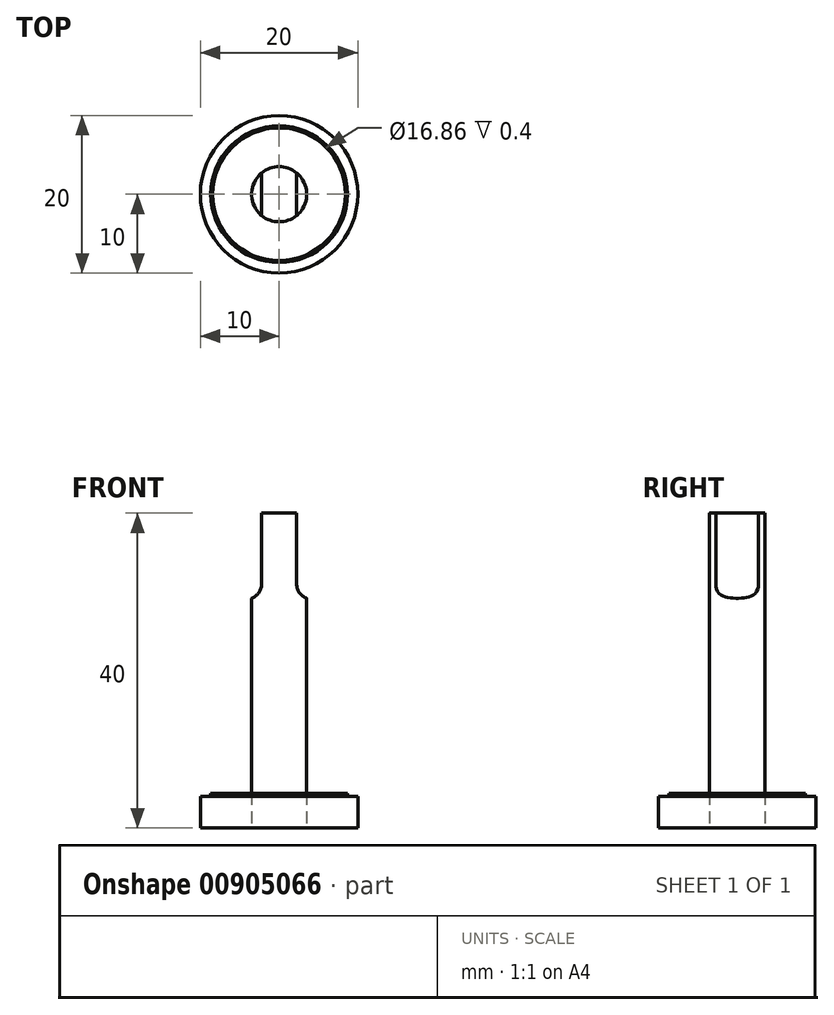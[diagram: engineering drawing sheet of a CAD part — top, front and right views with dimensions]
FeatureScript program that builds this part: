
annotation { "Feature Type Name" : "Feature", "Feature Type Description" : "" }
export const myFeature = defineFeature(function(context is Context, id is Id, definition is map)
    precondition{}
    {
        {
            var Q0;
            Q0=qCreatedBy(makeId("Top.planeOp"),FACE);
            var sketch = newSketch(context, id + "F0", { "sketchPlane" : qUnion([Q0])});
            skCircle(sketch, "E0", {"center": v(0, 0) * mm, "radius": 10 * mm});
            skCircle(sketch, "E1", {"center": v(0, 0) * mm, "radius": 3.5 * mm});
            skSolve(sketch);
        }
        {
            var Q0;
            Q0=makeQuery(id+"F0.imprint","IMPRINT",FACE,{"disambiguationData":[TD([[makeQuery(id+"F0.imprint","IMPRINT",EDGE,{"derivedFrom":sQuery(id+"F0.wireOp",EDGE,"E0")}),1.0]])]});
            var Q1;
            Q1=makeQuery(id+"F0.imprint","IMPRINT",FACE,{"disambiguationData":[TD([[makeQuery(id+"F0.imprint","IMPRINT",EDGE,{"derivedFrom":sQuery(id+"F0.wireOp",EDGE,"E1")}),-1.0]])]});
            var Q2;
            Q2=makeQuery(id+"F0.imprint","IMPRINT",FACE,{"disambiguationData":[TD([[makeQuery(id+"F0.imprint","IMPRINT",EDGE,{"derivedFrom":sQuery(id+"F0.wireOp",EDGE,"UNOtp6jB-zNbs-lB1D-Yq4t-WwCaiyIfWIL7")}),1.0]])]});
            var Q3;
            Q3=makeQuery(id+"F0.imprint","IMPRINT",FACE,{"disambiguationData":[TD([[makeQuery(id+"F0.imprint","IMPRINT",EDGE,{"derivedFrom":sQuery(id+"F0.wireOp",EDGE,"E1")}),1.0]])]});
            extrude(context, id + "F1", {"entities" : qUnion([Q0, Q1, Q2, Q3]), "depth" : 4 * mm, "offsetDistance" : 25 * mm});
        }
        {
            var Q0;
            Q0=makeQuery(id+"F0.imprint","IMPRINT",FACE,{"disambiguationData":[TD([[makeQuery(id+"F0.imprint","IMPRINT",EDGE,{"derivedFrom":sQuery(id+"F0.wireOp",EDGE,"E1")}),1.0]])]});
            extrude(context, id + "F2", {"entities" : qUnion([Q0]), "depth" : 40 * mm, "offsetDistance" : 25 * mm});
        }
        {
            var Q0;
            Q0=makeQuery(id+"F1.opExtrude","CAP_FACE",FACE,{"disambiguationData":[OSD([sQuery(id+"F0.wireOp",EDGE,"E0")])],"isStart":false});
            var sketch = newSketch(context, id + "F3", { "sketchPlane" : qUnion([Q0])});
            skCircle(sketch, "E2", {"center": v(0, 0) * mm, "radius": 8.68 * mm});
            skCircle(sketch, "E3", {"center": v(0, 0) * mm, "radius": 8.43 * mm});
            skSolve(sketch);
        }
        {
            var Q0;
            Q0=makeQuery(id+"F0.imprint","IMPRINT",FACE,{"disambiguationData":[TD([[makeQuery(id+"F0.imprint","IMPRINT",EDGE,{"derivedFrom":sQuery(id+"F0.wireOp",EDGE,"UNOtp6jB-zNbs-lB1D-Yq4t-WwCaiyIfWIL7")}),1.0]])]});
            var Q1;
            Q1 = qSketchRegion(id + "F3", true);
            extrude(context, id + "F4", {"entities" : qUnion([Q0, Q1]), "depth" : .4 * mm, "offsetDistance" : 25 * mm});
        }
        {
            var Q0;
            Q0=qCreatedBy(makeId("Front.planeOp"),FACE);
            var sketch = newSketch(context, id + "F5", { "sketchPlane" : qUnion([Q0])});
            skLineSegment(sketch, "E4.bottom", {"start": v(2.21, 41.1) * mm, "end": v(6.16, 41.1) * mm});
            skLineSegment(sketch, "E4.top", {"start": v(2.21, 31.03) * mm, "end": v(6.16, 31.03) * mm});
            skLineSegment(sketch, "E4.left", {"start": v(2.21, 41.1) * mm, "end": v(2.21, 31.03) * mm});
            skLineSegment(sketch, "E4.right", {"start": v(6.16, 41.1) * mm, "end": v(6.16, 31.03) * mm});
            skArc(sketch, "E5", {"start": v(2.21, 31.03) * mm, "mid": v(4.18, 29.06) * mm, "end": v(6.16, 31.03) * mm});
            skLineSegment(sketch, "E6", {"start": v(0, 44.26) * mm, "end": v(0, 26.14) * mm, "construction": true});
            skLineSegment(sketch, "E7.MirrorCS", {"start": v(-2.21, 41.1) * mm, "end": v(-2.21, 31.03) * mm});
            skLineSegment(sketch, "E8.MirrorCS", {"start": v(-2.21, 31.03) * mm, "end": v(-6.16, 31.03) * mm});
            skLineSegment(sketch, "E9.MirrorCS", {"start": v(-2.21, 41.1) * mm, "end": v(-6.16, 41.1) * mm});
            skLineSegment(sketch, "E10.MirrorCS", {"start": v(-6.16, 41.1) * mm, "end": v(-6.16, 31.03) * mm});
            skArc(sketch, "E11.MirrorCS", {"start": v(-2.21, 31.03) * mm, "mid": v(-4.18, 29.06) * mm, "end": v(-6.16, 31.03) * mm});
            skSolve(sketch);
        }
        {
            var Q0;
            Q0 = qSketchRegion(id + "F5", true);
            extrude(context, id + "F6", {"entities" : qUnion([Q0]), "operationType" : NewBodyOperationType.REMOVE, "endBound" : BoundingType.SYMMETRIC, "oppositeDirection" : true, "depth" : 25 * mm, "offsetDistance" : 25 * mm});
        }
    });
